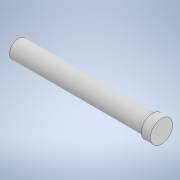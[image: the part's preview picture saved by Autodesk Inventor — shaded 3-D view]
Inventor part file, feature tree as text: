
AUTODESK INVENTOR PART (.ipt)
format: ipt  version: 2020 (Build 240168000, 168)  size: 101,376 bytes
history: native  units: mm
features: extrude x2, sketch x2
ambient origin geometry x8: Origin, YZ Plane, XZ Plane, XY Plane, X Axis, Y Axis, Z Axis, Center Point
bodies: Solid1 (feature_tree)
feature tree (4):
  extrude  "Extrusion1"  Depth=30.0mm TaperAngle=0.0deg
  extrude  "Extrusion2"  Depth=2.0mm TaperAngle=0.0deg
  sketch  "Sketch1"  dims[d0=4.0mm d1=30.0mm d2=0.0mm]
  sketch  "Sketch2"  dims[d3=5.0mm d4=2.0mm d5=0.0mm]
